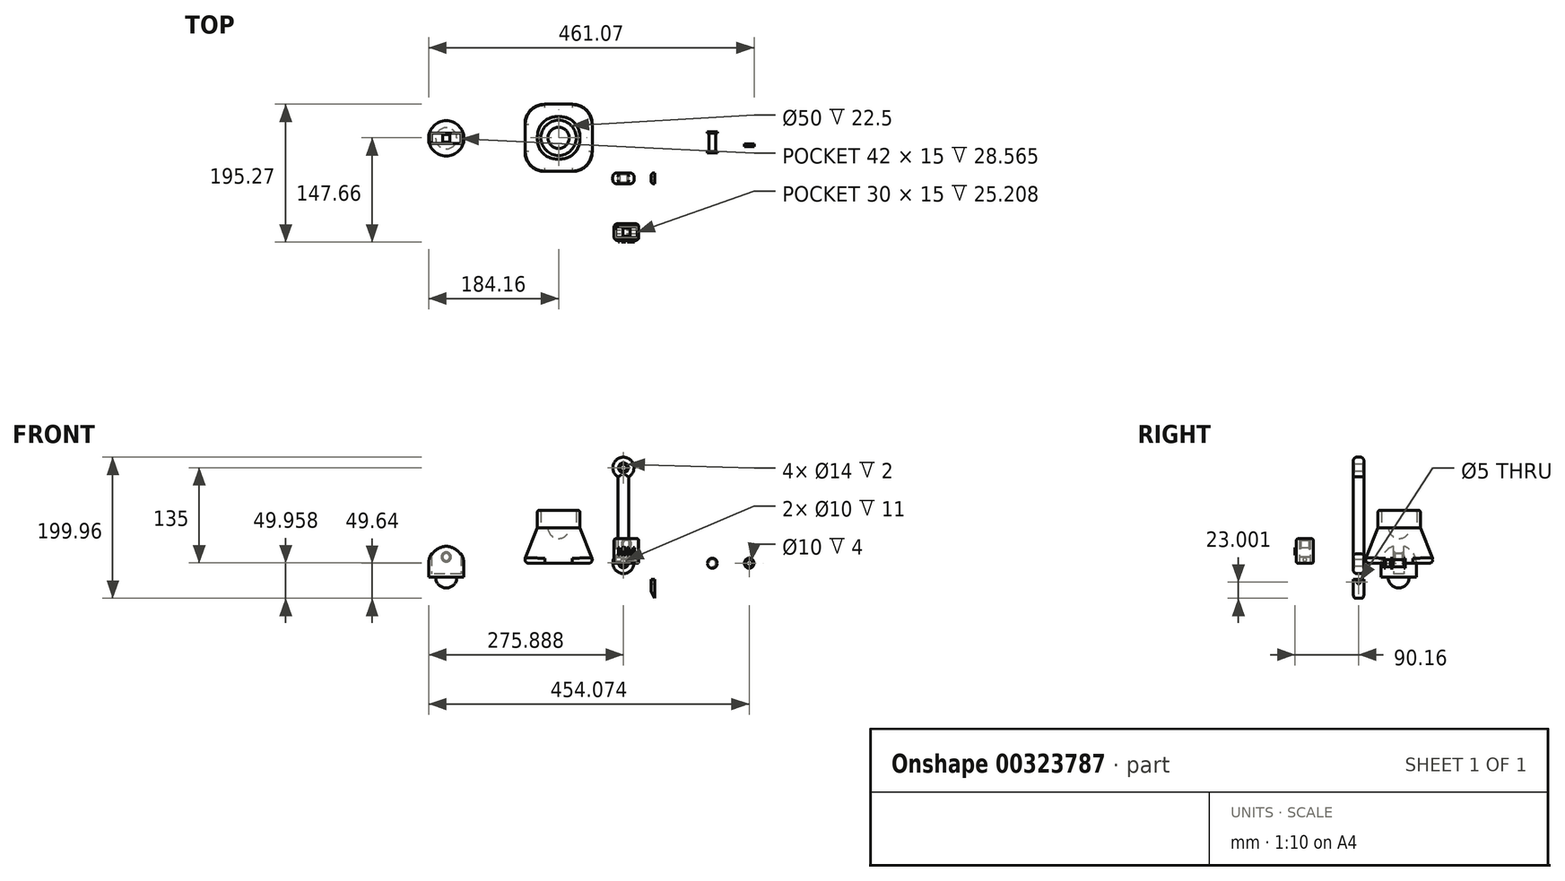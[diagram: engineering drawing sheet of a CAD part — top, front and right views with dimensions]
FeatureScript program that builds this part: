
annotation { "Feature Type Name" : "Feature", "Feature Type Description" : "" }
export const myFeature = defineFeature(function(context is Context, id is Id, definition is map)
    precondition{}
    {
        {
            var Q0;
            Q0=qCreatedBy(makeId("Top.planeOp"),FACE);
            var sketch = newSketch(context, id + "F0", { "sketchPlane" : qUnion([Q0])});
            skLineSegment(sketch, "E0.bottom", {"start": v(0, 0) * mm, "end": v(100, 0) * mm});
            skLineSegment(sketch, "E0.top", {"start": v(0, 100) * mm, "end": v(100, 100) * mm});
            skLineSegment(sketch, "E0.left", {"start": v(0, 0) * mm, "end": v(0, 100) * mm});
            skLineSegment(sketch, "E0.right", {"start": v(100, 0) * mm, "end": v(100, 100) * mm});
            skSolve(sketch);
        }
        {
            var Q0;
            Q0=makeQuery(id+"F0.imprint","IMPRINT",FACE,{"disambiguationData":[TD([[makeQuery(id+"F0.imprint","IMPRINT",EDGE,{"derivedFrom":sQuery(id+"F0.wireOp",EDGE,"E0.bottom")}),1.0]])]});
            cPlane(context, id + "F1", {"entities" : qUnion([Q0]), "cplaneType" : CPlaneType.OFFSET, "offset" : 50 * mm, "width" : 150 * mm, "height" : 150 * mm});
        }
        {
            var Q0;
            Q0=qCreatedBy(id+"F1.planeOp",FACE);
            var sketch = newSketch(context, id + "F2", { "sketchPlane" : qUnion([Q0])});
            skLineSegment(sketch, "E1.bottom", {"start": v(20, 80) * mm, "end": v(80, 80) * mm});
            skLineSegment(sketch, "E1.top", {"start": v(20, 20) * mm, "end": v(80, 20) * mm});
            skLineSegment(sketch, "E1.left", {"start": v(20, 80) * mm, "end": v(20, 20) * mm});
            skLineSegment(sketch, "E1.right", {"start": v(80, 80) * mm, "end": v(80, 20) * mm});
            skSolve(sketch);
        }
        {
            var Q0;
            Q0=makeQuery(id+"F0.imprint","IMPRINT",FACE,{"disambiguationData":[TD([[makeQuery(id+"F0.imprint","IMPRINT",EDGE,{"derivedFrom":sQuery(id+"F0.wireOp",EDGE,"E0.bottom")}),1.0]])]});
            var Q1;
            Q1=makeQuery(id+"F2.imprint","IMPRINT",FACE,{"disambiguationData":[TD([[makeQuery(id+"F2.imprint","IMPRINT",EDGE,{"derivedFrom":sQuery(id+"F2.wireOp",EDGE,"E1.bottom")}),-1.0]])]});
            loft(context, id + "F3", {"sheetProfilesArray" : [{ "sheetProfileEntities" : qUnion([Q0]) }, { "sheetProfileEntities" : qUnion([Q1]) }]});
        }
        {
            var Q0;
            Q0=makeQuery(id+"F3.opLoft","CAP_FACE",FACE,{"disambiguationData":[OSD([makeQuery(id+"F2.imprint","IMPRINT",FACE,{"disambiguationData":[TD([[makeQuery(id+"F2.imprint","IMPRINT",EDGE,{"derivedFrom":sQuery(id+"F2.wireOp",EDGE,"E1.bottom")}),-1.0]])]})])],"isStart":true});
            var sketch = newSketch(context, id + "F4", { "sketchPlane" : qUnion([Q0])});
            skLineSegment(sketch, "E2", {"start": v(50, 65) * mm, "end": v(50, 35) * mm});
            skArc(sketch, "E3", {"start": v(50, 35) * mm, "mid": v(65, 50) * mm, "end": v(50, 65) * mm});
            skPoint(sketch, "E4.orphan", {"position": v(50, 80) * mm});
            skPoint(sketch, "E5.orphan", {"position": v(50, 20) * mm});
            skSolve(sketch);
        }
        {
            var Q0;
            Q0=makeQuery(id+"F4.imprint","IMPRINT",FACE,{"disambiguationData":[TD([[makeQuery(id+"F4.imprint","IMPRINT",EDGE,{"derivedFrom":sQuery(id+"F4.wireOp",EDGE,"E2")}),1.0]])]});
            var Q1;
            Q1=sQuery(id+"F4.wireOp",EDGE,"E2");
            revolve(context, id + "F5", {"operationType" : NewBodyOperationType.REMOVE, "entities" : qUnion([Q0]), "axis" : qUnion([Q1]), "revolveType" : RevolveType.FULL, "oppositeDirection" : true});
        }
        {
            var Q0;
            Q0=makeQuery(id+"F3.opLoft","CAP_FACE",FACE,{"disambiguationData":[OSD([makeQuery(id+"F0.imprint","IMPRINT",FACE,{"disambiguationData":[TD([[makeQuery(id+"F0.imprint","IMPRINT",EDGE,{"derivedFrom":sQuery(id+"F0.wireOp",EDGE,"E0.bottom")}),1.0]])]})])],"isStart":true});
            fillet(context, id + "F6", {"entities" : qUnion([Q0]), "radius" : 5 * mm, "tangentPropagation" : true, "allowEdgeOverflow" : false});
        }
        {
            var Q0;
            Q0=makeQuery(id+"F3.opLoft","SWEPT_EDGE",EDGE,{"disambiguationData":[OSD([sQuery(id+"F0.wireOp",EDGE,"E0.bottom"),sQuery(id+"F0.wireOp",EDGE,"E0.right"),sQuery(id+"F2.wireOp",EDGE,"E1.top"),sQuery(id+"F2.wireOp",EDGE,"E1.right")])]});
            var Q1;
            Q1=makeQuery(id+"F3.opLoft","SWEPT_EDGE",EDGE,{"disambiguationData":[OSD([sQuery(id+"F0.wireOp",EDGE,"E0.top"),sQuery(id+"F0.wireOp",EDGE,"E0.right"),sQuery(id+"F2.wireOp",EDGE,"E1.bottom"),sQuery(id+"F2.wireOp",EDGE,"E1.right")])]});
            var Q2;
            Q2=makeQuery(id+"F3.opLoft","SWEPT_EDGE",EDGE,{"disambiguationData":[OSD([sQuery(id+"F0.wireOp",EDGE,"E0.top"),sQuery(id+"F0.wireOp",EDGE,"E0.left"),sQuery(id+"F2.wireOp",EDGE,"E1.bottom"),sQuery(id+"F2.wireOp",EDGE,"E1.left")])]});
            var Q3;
            Q3=makeQuery(id+"F3.opLoft","SWEPT_EDGE",EDGE,{"disambiguationData":[OSD([sQuery(id+"F0.wireOp",EDGE,"E0.bottom"),sQuery(id+"F0.wireOp",EDGE,"E0.left"),sQuery(id+"F2.wireOp",EDGE,"E1.top"),sQuery(id+"F2.wireOp",EDGE,"E1.left")])]});
            fillet(context, id + "F7", {"entities" : qUnion([Q0, Q1, Q2, Q3]), "radius" : 30 * mm, "tangentPropagation" : true, "allowEdgeOverflow" : false});
        }
        {
            var Q0;
            Q0=qCreatedBy(makeId("Top.planeOp"),FACE);
            var sketch = newSketch(context, id + "F8", { "sketchPlane" : qUnion([Q0])});
            skArc(sketch, "E6", {"start": v(184.89, 22.61) * mm, "mid": v(199.89, 37.61) * mm, "end": v(184.89, 52.61) * mm});
            skLineSegment(sketch, "E7", {"start": v(184.89, 22.61) * mm, "end": v(184.89, 52.61) * mm});
            skSolve(sketch);
        }
        {
            var Q0;
            Q0=qCreatedBy(makeId("Top.planeOp"),FACE);
            cPlane(context, id + "F9", {"entities" : qUnion([Q0]), "cplaneType" : CPlaneType.OFFSET, "offset" : 10 * mm, "width" : 150 * mm, "height" : 150 * mm});
        }
        {
            var Q0;
            Q0=qCreatedBy(id+"F9.planeOp",FACE);
            var sketch = newSketch(context, id + "F10", { "sketchPlane" : qUnion([Q0])});
            skLineSegment(sketch, "E8.bottom", {"start": v(177.39, 45.11) * mm, "end": v(192.39, 45.11) * mm});
            skLineSegment(sketch, "E8.top", {"start": v(177.39, 30.11) * mm, "end": v(192.39, 30.11) * mm});
            skLineSegment(sketch, "E8.left", {"start": v(177.39, 45.11) * mm, "end": v(177.39, 30.11) * mm});
            skLineSegment(sketch, "E8.right", {"start": v(192.39, 45.11) * mm, "end": v(192.39, 30.11) * mm});
            skSolve(sketch);
        }
        {
            var Q0;
            Q0=makeQuery(id+"F8.imprint","IMPRINT",FACE,{"disambiguationData":[TD([[makeQuery(id+"F8.imprint","IMPRINT",EDGE,{"derivedFrom":sQuery(id+"F8.wireOp",EDGE,"E6")}),1.0]])]});
            var Q1;
            Q1=sQuery(id+"F8.wireOp",EDGE,"E7");
            revolve(context, id + "F11", {"entities" : qUnion([Q0]), "axis" : qUnion([Q1]), "revolveType" : RevolveType.FULL});
        }
        {
            var Q0;
            Q0=qSketchRegion(id+"F10",true);
            extrude(context, id + "F12", {"entities" : qUnion([Q0]), "operationType" : NewBodyOperationType.ADD, "depth" : 120 * mm});
        }
        {
            var Q0;
            Q0=makeQuery(id+"F12.boolean.opBoolean","INTERSECT",EDGE,{"derivedFrom":[makeQuery(id+"F11.opRevolve","SWEPT_FACE",FACE,{"disambiguationData":[OSD([sQuery(id+"F8.wireOp",EDGE,"E6")])]}),makeQuery(id+"F12.opExtrude","SWEPT_FACE",FACE,{"disambiguationData":[OSD([sQuery(id+"F10.wireOp",EDGE,"E8.right")])]})]});
            var Q1;
            Q1=makeQuery(id+"F12.boolean.opBoolean","INTERSECT",EDGE,{"derivedFrom":[makeQuery(id+"F11.opRevolve","SWEPT_FACE",FACE,{"disambiguationData":[OSD([sQuery(id+"F8.wireOp",EDGE,"E6")])]}),makeQuery(id+"F12.opExtrude","SWEPT_FACE",FACE,{"disambiguationData":[OSD([sQuery(id+"F10.wireOp",EDGE,"E8.top")])]})]});
            var Q2;
            Q2=makeQuery(id+"F12.boolean.opBoolean","INTERSECT",EDGE,{"derivedFrom":[makeQuery(id+"F11.opRevolve","SWEPT_FACE",FACE,{"disambiguationData":[OSD([sQuery(id+"F8.wireOp",EDGE,"E6")])]}),makeQuery(id+"F12.opExtrude","SWEPT_FACE",FACE,{"disambiguationData":[OSD([sQuery(id+"F10.wireOp",EDGE,"E8.bottom")])]})]});
            var Q3;
            Q3=makeQuery(id+"F12.boolean.opBoolean","INTERSECT",EDGE,{"derivedFrom":[makeQuery(id+"F11.opRevolve","SWEPT_FACE",FACE,{"disambiguationData":[OSD([sQuery(id+"F8.wireOp",EDGE,"E6")])]}),makeQuery(id+"F12.opExtrude","SWEPT_FACE",FACE,{"disambiguationData":[OSD([sQuery(id+"F10.wireOp",EDGE,"E8.left")])]})]});
            var Q4;
            Q4=makeQuery(id+"F12.opExtrude","SWEPT_EDGE",EDGE,{"disambiguationData":[OSD([sQuery(id+"F10.wireOp",EDGE,"E8.bottom"),sQuery(id+"F10.wireOp",EDGE,"E8.left")])]});
            var Q5;
            Q5=makeQuery(id+"F12.opExtrude","SWEPT_EDGE",EDGE,{"disambiguationData":[OSD([sQuery(id+"F10.wireOp",EDGE,"E8.bottom"),sQuery(id+"F10.wireOp",EDGE,"E8.right")])]});
            var Q6;
            Q6=makeQuery(id+"F12.opExtrude","SWEPT_EDGE",EDGE,{"disambiguationData":[OSD([sQuery(id+"F10.wireOp",EDGE,"E8.top"),sQuery(id+"F10.wireOp",EDGE,"E8.right")])]});
            var Q7;
            Q7=makeQuery(id+"F12.opExtrude","SWEPT_EDGE",EDGE,{"disambiguationData":[OSD([sQuery(id+"F10.wireOp",EDGE,"E8.top"),sQuery(id+"F10.wireOp",EDGE,"E8.left")])]});
            fillet(context, id + "F13", {"entities" : qUnion([Q0, Q1, Q2, Q3, Q4, Q5, Q6, Q7]), "radius" : 5 * mm, "tangentPropagation" : true, "allowEdgeOverflow" : false});
        }
        {
            var Q0;
            Q0=makeQuery(id+"F12.opExtrude","CAP_EDGE",EDGE,{"disambiguationData":[OSD([sQuery(id+"F10.wireOp",EDGE,"E8.right")])],"isStart":false});
            cPoint(context, id + "F14", {"entities" : qUnion([Q0]), "parameter" : 0.5});
        }
        {
            var Q0;
            Q0=makeQuery(id+"F12.opExtrude","CAP_EDGE",EDGE,{"disambiguationData":[OSD([sQuery(id+"F10.wireOp",EDGE,"E8.left")])],"isStart":false});
            cPoint(context, id + "F15", {"entities" : qUnion([Q0]), "parameter" : 0.5});
        }
        {
            var Q0;
            {var subQ0=makeQuery(id+"F12.opExtrude","SWEPT_FACE",FACE,{"disambiguationData":[OSD([sQuery(id+"F10.wireOp",EDGE,"E8.left")])]});Q0=makeQuery(id+"F13.opFillet","BLEND_EDGE",EDGE,{"blendedFrom":[makeQuery(id+"F12.boolean.opBoolean","INTERSECT",EDGE,{"derivedFrom":[makeQuery(id+"F11.opRevolve","SWEPT_FACE",FACE,{"disambiguationData":[OSD([sQuery(id+"F8.wireOp",EDGE,"E6")])]}),subQ0]}),subQ0],"blendedInto":[subQ0]});}
            cPoint(context, id + "F16", {"entities" : qUnion([Q0]), "parameter" : 0.5});
        }
        {
            var Q0;
            Q0=qCreatedBy(id+"F14",VERTEX);
            var Q1;
            Q1=qCreatedBy(id+"F15",VERTEX);
            var Q2;
            Q2=qCreatedBy(id+"F16",VERTEX);
            cPlane(context, id + "F17", {"entities" : qUnion([Q0, Q1, Q2]), "cplaneType" : CPlaneType.THREE_POINT, "offset" : 25 * mm, "width" : 150 * mm, "height" : 150 * mm});
        }
        {
            var Q0;
            Q0=qCreatedBy(id+"F17.planeOp",FACE);
            var sketch = newSketch(context, id + "F18", { "sketchPlane" : qUnion([Q0])});
            skCircle(sketch, "E9", {"center": v(-184.89, 137.5) * mm, "radius": 15 * mm});
            skSolve(sketch);
        }
        {
            var Q0;
            Q0=makeQuery(id+"F18.imprint","IMPRINT",FACE,{"disambiguationData":[TD([[makeQuery(id+"F18.imprint","IMPRINT",EDGE,{"derivedFrom":sQuery(id+"F18.wireOp",EDGE,"E9")}),1.0]])]});
            extrude(context, id + "F19", {"entities" : qUnion([Q0]), "operationType" : NewBodyOperationType.ADD, "depth" : 15 * mm, "symmetric" : true});
        }
        {
            var Q0;
            Q0=makeQuery(id+"F19.opExtrude","CAP_EDGE",EDGE,{"disambiguationData":[OSD([sQuery(id+"F18.wireOp",EDGE,"E9")])],"isStart":true});
            var Q1;
            Q1=makeQuery(id+"F19.opExtrude","CAP_EDGE",EDGE,{"disambiguationData":[OSD([sQuery(id+"F18.wireOp",EDGE,"E9")])],"isStart":false});
            fillet(context, id + "F20", {"entities" : qUnion([Q0, Q1]), "radius" : 5 * mm, "tangentPropagation" : true, "allowEdgeOverflow" : false});
        }
        {
            var Q0;
            Q0=makeQuery(id+"F19.boolean.opBoolean","MERGE",FACE,{"derivedFrom":[makeQuery(id+"F12.opExtrude","SWEPT_FACE",FACE,{"disambiguationData":[OSD([sQuery(id+"F10.wireOp",EDGE,"E8.top")])]}),makeQuery(id+"F19.opExtrude","CAP_FACE",FACE,{"disambiguationData":[OSD([sQuery(id+"F18.wireOp",EDGE,"E9")])],"isStart":true})]});
            var sketch = newSketch(context, id + "F21", { "sketchPlane" : qUnion([Q0])});
            skCircle(sketch, "E10", {"center": v(184.89, 137.5) * mm, "radius": 5 * mm});
            skCircle(sketch, "E11", {"center": v(184.89, 137.5) * mm, "radius": 7 * mm});
            skSolve(sketch);
        }
        {
            var Q0;
            Q0=sQuery(id+"F21.wireOp",VERTEX,"E10.center");
            var Q1;
            Q1=makeQuery(id+"F11.opRevolve","SWEPT_BODY",BODY,{"disambiguationData":[OSD([sQuery(id+"F8.wireOp",EDGE,"E6"),sQuery(id+"F8.wireOp",EDGE,"E7")])]});
            hole(context, id + "F22", {"style" : HoleStyle.SIMPLE, "endStyle" : HoleEndStyle.THROUGH, "holeDiameter" : 10 * mm, "tappedDepth" : 12 * mm, "tapClearance" : 3, "locations" : qUnion([Q0]), "scope" : qUnion([Q1])});
        }
        {
            var Q0;
            Q0=makeQuery(id+"F19.boolean.opBoolean","MERGE",FACE,{"derivedFrom":[makeQuery(id+"F12.opExtrude","SWEPT_FACE",FACE,{"disambiguationData":[OSD([sQuery(id+"F10.wireOp",EDGE,"E8.bottom")])]}),makeQuery(id+"F19.opExtrude","CAP_FACE",FACE,{"disambiguationData":[OSD([sQuery(id+"F18.wireOp",EDGE,"E9")])],"isStart":false})]});
            var sketch = newSketch(context, id + "F23", { "sketchPlane" : qUnion([Q0])});
            skCircle(sketch, "E12", {"center": v(-184.89, 137.5) * mm, "radius": 7 * mm});
            skSolve(sketch);
        }
        {
            var Q0;
            Q0=qSketchRegion(id+"F21",true);
            var Q1;
            Q1=qSketchRegion(id+"F23",true);
            extrude(context, id + "F24", {"entities" : qUnion([Q0, Q1]), "operationType" : NewBodyOperationType.REMOVE, "oppositeDirection" : true, "depth" : 2 * mm, "hasSecondDirection" : true, "secondDirectionOppositeDirection" : false, "secondDirectionDepth" : 2 * mm});
        }
        {
            var Q0;
            Q0=qCreatedBy(makeId("Top.planeOp"),FACE);
            var sketch = newSketch(context, id + "F25", { "sketchPlane" : qUnion([Q0])});
            skLineSegment(sketch, "E13.bottom", {"start": v(267.71, 58.7) * mm, "end": v(272.71, 58.7) * mm});
            skLineSegment(sketch, "E13.top", {"start": v(267.71, 28.7) * mm, "end": v(272.71, 28.7) * mm});
            skLineSegment(sketch, "E13.left", {"start": v(267.71, 58.7) * mm, "end": v(267.71, 28.7) * mm});
            skLineSegment(sketch, "E13.right", {"start": v(272.71, 56.7) * mm, "end": v(272.71, 30.7) * mm});
            skLineSegment(sketch, "E14.bottom", {"start": v(272.71, 58.7) * mm, "end": v(274.71, 58.7) * mm});
            skLineSegment(sketch, "E14.top", {"start": v(272.71, 56.7) * mm, "end": v(274.71, 56.7) * mm});
            skLineSegment(sketch, "E14.right", {"start": v(274.71, 58.7) * mm, "end": v(274.71, 56.7) * mm});
            skLineSegment(sketch, "E15.bottom", {"start": v(272.71, 28.7) * mm, "end": v(274.71, 28.7) * mm});
            skLineSegment(sketch, "E15.top", {"start": v(272.71, 30.7) * mm, "end": v(274.71, 30.7) * mm});
            skLineSegment(sketch, "E15.right", {"start": v(274.71, 28.7) * mm, "end": v(274.71, 30.7) * mm});
            skSolve(sketch);
        }
        {
            var Q0;
            Q0=makeQuery(id+"F25.imprint","IMPRINT",FACE,{"disambiguationData":[TD([[makeQuery(id+"F25.imprint","IMPRINT",EDGE,{"derivedFrom":sQuery(id+"F25.wireOp",EDGE,"E13.bottom")}),-1.0]])]});
            var Q1;
            Q1=sQuery(id+"F25.wireOp",EDGE,"E13.left");
            revolve(context, id + "F26", {"entities" : qUnion([Q0]), "axis" : qUnion([Q1]), "revolveType" : RevolveType.FULL});
        }
        {
            var Q0;
            Q0=qCreatedBy(id+"F17.planeOp",FACE);
            var sketch = newSketch(context, id + "F27", { "sketchPlane" : qUnion([Q0])});
            skCircle(sketch, "E16", {"center": v(-319.91, 0) * mm, "radius": 7 * mm});
            skCircle(sketch, "E17", {"center": v(-319.91, 0) * mm, "radius": 5 * mm});
            skSolve(sketch);
        }
        {
            var Q0;
            Q0=qSketchRegion(id+"F27",true);
            extrude(context, id + "F28", {"entities" : qUnion([Q0]), "depth" : 4 * mm});
        }
        {
            var Q0;
            Q0=qCreatedBy(makeId("Top.planeOp"),FACE);
            var sketch = newSketch(context, id + "F29", { "sketchPlane" : qUnion([Q0])});
            skArc(sketch, "E18", {"start": v(-109.16, 24.23) * mm, "mid": v(-84.16, 49.23) * mm, "end": v(-109.16, 74.23) * mm});
            skLineSegment(sketch, "E19", {"start": v(-109.16, 74.23) * mm, "end": v(-109.16, 24.23) * mm});
            skSolve(sketch);
        }
        {
            var Q0;
            Q0=makeQuery(id+"F29.imprint","IMPRINT",FACE,{"disambiguationData":[TD([[makeQuery(id+"F29.imprint","IMPRINT",EDGE,{"derivedFrom":sQuery(id+"F29.wireOp",EDGE,"E18")}),1.0]])]});
            var Q1;
            Q1=sQuery(id+"F29.wireOp",EDGE,"E19");
            revolve(context, id + "F30", {"entities" : qUnion([Q0]), "axis" : qUnion([Q1]), "revolveType" : RevolveType.ONE_DIRECTION, "angle" : 180 * degree});
        }
        {
            var Q0;
            Q0=qCreatedBy(makeId("Front.planeOp"),FACE);
            var sketch = newSketch(context, id + "F31", { "sketchPlane" : qUnion([Q0])});
            skLineSegment(sketch, "E20.left", {"start": v(134.23, 122.33) * mm, "end": v(134.23, 13.3) * mm});
            skLineSegment(sketch, "E20.right", {"start": v(149.23, 122.33) * mm, "end": v(149.23, 13.3) * mm});
            skArc(sketch, "E21", {"start": v(149.23, 122.33) * mm, "mid": v(141.73, 150.32) * mm, "end": v(134.23, 122.33) * mm});
            skArc(sketch, "E22", {"start": v(134.23, 13.3) * mm, "mid": v(141.73, -14.68) * mm, "end": v(149.23, 13.3) * mm});
            skSolve(sketch);
        }
        {
            var Q0;
            Q0=makeQuery(id+"F31.imprint","IMPRINT",FACE,{"disambiguationData":[TD([[makeQuery(id+"F31.imprint","IMPRINT",EDGE,{"derivedFrom":sQuery(id+"F31.wireOp",EDGE,"E20.left")}),1.0]])]});
            extrude(context, id + "F32", {"entities" : qUnion([Q0]), "depth" : 15 * mm});
        }
        {
            var Q0;
            Q0=makeQuery(id+"F32.opExtrude","CAP_FACE",FACE,{"disambiguationData":[OSD([sQuery(id+"F31.wireOp",EDGE,"E20.left"),sQuery(id+"F31.wireOp",EDGE,"E20.right"),sQuery(id+"F31.wireOp",EDGE,"E21"),sQuery(id+"F31.wireOp",EDGE,"E22")])],"isStart":false});
            var Q1;
            Q1=makeQuery(id+"F32.opExtrude","CAP_FACE",FACE,{"disambiguationData":[OSD([sQuery(id+"F31.wireOp",EDGE,"E20.left"),sQuery(id+"F31.wireOp",EDGE,"E20.right"),sQuery(id+"F31.wireOp",EDGE,"E21"),sQuery(id+"F31.wireOp",EDGE,"E22")])],"isStart":true});
            fillet(context, id + "F33", {"entities" : qUnion([Q0, Q1]), "radius" : 5 * mm, "tangentPropagation" : true, "allowEdgeOverflow" : false});
        }
        {
            var Q0;
            Q0=makeQuery(id+"F32.opExtrude","CAP_FACE",FACE,{"disambiguationData":[OSD([sQuery(id+"F31.wireOp",EDGE,"E20.left"),sQuery(id+"F31.wireOp",EDGE,"E20.right"),sQuery(id+"F31.wireOp",EDGE,"E21"),sQuery(id+"F31.wireOp",EDGE,"E22")])],"isStart":false});
            var sketch = newSketch(context, id + "F34", { "sketchPlane" : qUnion([Q0])});
            skCircle(sketch, "E23", {"center": v(141.73, 135.32) * mm, "radius": 5 * mm});
            skCircle(sketch, "E24", {"center": v(141.73, 0.32) * mm, "radius": 5 * mm});
            skCircle(sketch, "E25", {"center": v(141.73, 135.32) * mm, "radius": 7 * mm});
            skCircle(sketch, "E26", {"center": v(141.73, 0.32) * mm, "radius": 7 * mm});
            skSolve(sketch);
        }
        {
            var Q0;
            Q0=makeQuery(id+"F34.imprint","IMPRINT",FACE,{"disambiguationData":[TD([[makeQuery(id+"F34.imprint","IMPRINT",EDGE,{"derivedFrom":sQuery(id+"F34.wireOp",EDGE,"E23")}),1.0]])]});
            var Q1;
            Q1=makeQuery(id+"F34.imprint","IMPRINT",FACE,{"disambiguationData":[TD([[makeQuery(id+"F34.imprint","IMPRINT",EDGE,{"derivedFrom":sQuery(id+"F34.wireOp",EDGE,"E24")}),1.0]])]});
            extrude(context, id + "F35", {"entities" : qUnion([Q0, Q1]), "operationType" : NewBodyOperationType.REMOVE, "endBound" : BoundingType.THROUGH_ALL, "oppositeDirection" : true, "depth" : 25 * mm});
        }
        {
            var Q0;
            Q0=qSketchRegion(id+"F34",true);
            extrude(context, id + "F36", {"entities" : qUnion([Q0]), "operationType" : NewBodyOperationType.REMOVE, "oppositeDirection" : true, "depth" : 2 * mm});
        }
        {
            var Q0;
            Q0=makeQuery(id+"F32.opExtrude","CAP_FACE",FACE,{"disambiguationData":[OSD([sQuery(id+"F31.wireOp",EDGE,"E20.left"),sQuery(id+"F31.wireOp",EDGE,"E20.right"),sQuery(id+"F31.wireOp",EDGE,"E21"),sQuery(id+"F31.wireOp",EDGE,"E22")])],"isStart":true});
            var sketch = newSketch(context, id + "F37", { "sketchPlane" : qUnion([Q0])});
            skCircle(sketch, "E27", {"center": v(-141.73, 135.32) * mm, "radius": 7 * mm});
            skCircle(sketch, "E28", {"center": v(-141.73, 0.32) * mm, "radius": 7 * mm});
            skSolve(sketch);
        }
        {
            var Q0;
            Q0=qSketchRegion(id+"F37",true);
            extrude(context, id + "F38", {"entities" : qUnion([Q0]), "operationType" : NewBodyOperationType.REMOVE, "oppositeDirection" : true, "depth" : 2 * mm});
        }
        {
            var Q0;
            Q0=makeQuery(id+"F30.opRevolve","CAP_FACE",FACE,{"disambiguationData":[OSD([sQuery(id+"F29.wireOp",EDGE,"E18"),sQuery(id+"F29.wireOp",EDGE,"E19")])],"isStart":true});
            var sketch = newSketch(context, id + "F39", { "sketchPlane" : qUnion([Q0])});
            skLineSegment(sketch, "E29.bottom", {"start": v(-88.16, -56.73) * mm, "end": v(-130.16, -56.73) * mm});
            skLineSegment(sketch, "E29.top", {"start": v(-88.16, -41.73) * mm, "end": v(-130.16, -41.73) * mm});
            skLineSegment(sketch, "E29.left", {"start": v(-88.16, -56.73) * mm, "end": v(-88.16, -41.73) * mm});
            skLineSegment(sketch, "E29.right", {"start": v(-130.16, -56.73) * mm, "end": v(-130.16, -41.73) * mm});
            skSolve(sketch);
        }
        {
            var Q0;
            Q0=makeQuery(id+"F39.imprint","IMPRINT",FACE,{"disambiguationData":[TD([[makeQuery(id+"F39.imprint","IMPRINT",EDGE,{"derivedFrom":sQuery(id+"F39.wireOp",EDGE,"E29.bottom")}),1.0]])]});
            var Q1;
            Q1=makeQuery(id+"F39.imprint","IMPRINT",FACE,{"disambiguationData":[TD([[makeQuery(id+"F39.imprint","IMPRINT",EDGE,{"derivedFrom":sQuery(id+"F39.wireOp",EDGE,"E29.bottom")}),-1.0]])]});
            extrude(context, id + "F40", {"entities" : qUnion([Q0, Q1]), "operationType" : NewBodyOperationType.ADD, "depth" : 20 * mm});
        }
        {
            var Q0;
            Q0=makeQuery(id+"F40.opExtrude","CAP_FACE",FACE,{"disambiguationData":[OSD([sQuery(id+"F29.wireOp",EDGE,"E18")])],"isStart":false});
            var sketch = newSketch(context, id + "F41", { "sketchPlane" : qUnion([Q0])});
            skArc(sketch, "E30", {"start": v(-109.16, -34.23) * mm, "mid": v(-124.16, -49.23) * mm, "end": v(-109.16, -64.23) * mm});
            skLineSegment(sketch, "E31", {"start": v(-109.16, -64.23) * mm, "end": v(-109.16, -34.23) * mm});
            skSolve(sketch);
        }
        {
            var Q0;
            Q0=makeQuery(id+"F41.imprint","IMPRINT",FACE,{"disambiguationData":[TD([[makeQuery(id+"F41.imprint","IMPRINT",EDGE,{"derivedFrom":sQuery(id+"F41.wireOp",EDGE,"E30")}),1.0]])]});
            var Q1;
            Q1=sQuery(id+"F41.wireOp",EDGE,"E31");
            revolve(context, id + "F42", {"operationType" : NewBodyOperationType.ADD, "entities" : qUnion([Q0]), "axis" : qUnion([Q1]), "revolveType" : RevolveType.FULL});
        }
        {
            var Q0;
            Q0=qSketchRegion(id+"F39",true);
            extrude(context, id + "F43", {"entities" : qUnion([Q0]), "operationType" : NewBodyOperationType.REMOVE, "endBound" : BoundingType.THROUGH_ALL, "oppositeDirection" : true, "depth" : 25 * mm, "hasSecondDirection" : true, "secondDirectionOppositeDirection" : false, "secondDirectionDepth" : 15 * mm});
        }
        {
            var Q0;
            Q0=makeQuery(id+"F43.boolean.opBoolean","COPY",FACE,{"derivedFrom":makeQuery(id+"F43.opExtrude","SWEPT_FACE",FACE,{"disambiguationData":[OSD([sQuery(id+"F39.wireOp",EDGE,"E29.top")])]})});
            var sketch = newSketch(context, id + "F44", { "sketchPlane" : qUnion([Q0])});
            skCircle(sketch, "E32", {"center": v(109.16, 8.85) * mm, "radius": 7 * mm});
            skPoint(sketch, "E32.centerSnap0", {"position": v(109.16, 23.85) * mm});
            skPoint(sketch, "E32.centerSnap1", {"position": v(130.16, -1.85) * mm});
            skSolve(sketch);
        }
        {
            var Q0;
            Q0=makeQuery(id+"F44.imprint","IMPRINT",FACE,{"disambiguationData":[TD([[makeQuery(id+"F44.imprint","IMPRINT",EDGE,{"derivedFrom":sQuery(id+"F44.wireOp",EDGE,"E32")}),1.0]])]});
            extrude(context, id + "F45", {"entities" : qUnion([Q0]), "operationType" : NewBodyOperationType.ADD, "depth" : 2 * mm});
        }
        {
            var Q0;
            Q0=makeQuery(id+"F45.opExtrude","CAP_FACE",FACE,{"disambiguationData":[OSD([sQuery(id+"F44.wireOp",EDGE,"E32")])],"isStart":false});
            var sketch = newSketch(context, id + "F46", { "sketchPlane" : qUnion([Q0])});
            skCircle(sketch, "E33", {"center": v(109.16, 8.85) * mm, "radius": 5 * mm});
            skSolve(sketch);
        }
        {
            var Q0;
            Q0=makeQuery(id+"F46.imprint","IMPRINT",FACE,{"disambiguationData":[TD([[makeQuery(id+"F46.imprint","IMPRINT",EDGE,{"derivedFrom":sQuery(id+"F46.wireOp",EDGE,"E33")}),1.0]])]});
            extrude(context, id + "F47", {"entities" : qUnion([Q0]), "operationType" : NewBodyOperationType.ADD, "endBound" : BoundingType.UP_TO_NEXT, "depth" : 25 * mm});
        }
        {
            var Q0;
            Q0=qCreatedBy(makeId("Top.planeOp"),FACE);
            var sketch = newSketch(context, id + "F48", { "sketchPlane" : qUnion([Q0])});
            skLineSegment(sketch, "E34.bottom", {"start": v(203.21, -84.7) * mm, "end": v(208.21, -84.7) * mm});
            skLineSegment(sketch, "E34.top", {"start": v(203.21, -99.7) * mm, "end": v(208.21, -99.7) * mm});
            skLineSegment(sketch, "E34.left", {"start": v(198.21, -89.7) * mm, "end": v(198.21, -94.7) * mm});
            skLineSegment(sketch, "E34.right", {"start": v(213.21, -89.7) * mm, "end": v(213.21, -94.7) * mm});
            skPoint(sketch, "E35.visualSharp", {"position": v(198.21, -84.7) * mm});
            skArc(sketch, "E35.filletArc", {"start": v(203.21, -84.7) * mm, "mid": v(199.68, -86.16) * mm, "end": v(198.21, -89.7) * mm});
            skPoint(sketch, "E36.visualSharp", {"position": v(213.21, -84.7) * mm});
            skArc(sketch, "E36.filletArc", {"start": v(213.21, -89.7) * mm, "mid": v(211.75, -86.16) * mm, "end": v(208.21, -84.7) * mm});
            skPoint(sketch, "E37.visualSharp", {"position": v(213.21, -99.7) * mm});
            skArc(sketch, "E37.filletArc", {"start": v(208.21, -99.7) * mm, "mid": v(211.75, -98.23) * mm, "end": v(213.21, -94.7) * mm});
            skPoint(sketch, "E38.visualSharp", {"position": v(198.21, -99.7) * mm});
            skArc(sketch, "E38.filletArc", {"start": v(198.21, -94.7) * mm, "mid": v(199.68, -98.23) * mm, "end": v(203.21, -99.7) * mm});
            skLineSegment(sketch, "E39.bottom", {"start": v(192.71, -74.2) * mm, "end": v(218.71, -74.2) * mm});
            skLineSegment(sketch, "E39.top", {"start": v(192.71, -110.2) * mm, "end": v(218.71, -110.2) * mm});
            skLineSegment(sketch, "E39.left", {"start": v(187.71, -79.2) * mm, "end": v(187.71, -105.2) * mm});
            skLineSegment(sketch, "E39.right", {"start": v(223.71, -79.2) * mm, "end": v(223.71, -105.2) * mm});
            skPoint(sketch, "E40.visualSharp", {"position": v(187.71, -74.2) * mm});
            skArc(sketch, "E40.filletArc", {"start": v(192.71, -74.2) * mm, "mid": v(189.18, -75.66) * mm, "end": v(187.71, -79.2) * mm});
            skPoint(sketch, "E41.visualSharp", {"position": v(223.71, -74.2) * mm});
            skArc(sketch, "E41.filletArc", {"start": v(223.71, -79.2) * mm, "mid": v(222.25, -75.66) * mm, "end": v(218.71, -74.2) * mm});
            skPoint(sketch, "E42.visualSharp", {"position": v(223.71, -110.2) * mm});
            skArc(sketch, "E42.filletArc", {"start": v(218.71, -110.2) * mm, "mid": v(222.25, -108.73) * mm, "end": v(223.71, -105.2) * mm});
            skPoint(sketch, "E43.visualSharp", {"position": v(187.71, -110.2) * mm});
            skArc(sketch, "E43.filletArc", {"start": v(187.71, -105.2) * mm, "mid": v(189.18, -108.73) * mm, "end": v(192.71, -110.2) * mm});
            skSolve(sketch);
        }
        {
            var Q0;
            Q0=makeQuery(id+"F48.imprint","IMPRINT",FACE,{"disambiguationData":[TD([[makeQuery(id+"F48.imprint","IMPRINT",EDGE,{"derivedFrom":sQuery(id+"F48.wireOp",EDGE,"E34.bottom")}),1.0]])]});
            extrude(context, id + "F49", {"entities" : qUnion([Q0]), "depth" : 20 * mm});
        }
        {
            var Q0;
            Q0=makeQuery(id+"F49.opExtrude","CAP_EDGE",EDGE,{"disambiguationData":[OSD([sQuery(id+"F48.wireOp",EDGE,"E39.left")])],"isStart":false});
            fillet(context, id + "F50", {"entities" : qUnion([Q0]), "radius" : 10 * mm, "tangentPropagation" : true, "allowEdgeOverflow" : false});
        }
        {
            var Q0;
            Q0=makeQuery(id+"F49.opExtrude","CAP_EDGE",EDGE,{"disambiguationData":[OSD([sQuery(id+"F48.wireOp",EDGE,"E34.top")])],"isStart":true});
            var Q1;
            Q1=makeQuery(id+"F49.opExtrude","CAP_EDGE",EDGE,{"disambiguationData":[OSD([sQuery(id+"F48.wireOp",EDGE,"E37.filletArc")])],"isStart":true});
            fillet(context, id + "F51", {"entities" : qUnion([Q0, Q1]), "radius" : 5 * mm, "tangentPropagation" : true, "allowEdgeOverflow" : false});
        }
        {
            var Q0;
            Q0=makeQuery(id+"F11.opRevolve","SWEPT_BODY",BODY,{"disambiguationData":[OSD([sQuery(id+"F8.wireOp",EDGE,"E6"),sQuery(id+"F8.wireOp",EDGE,"E7")])]});
            deleteBodies(context, id + "F52", {"entities" : qUnion([Q0])});
        }
        {
            var Q0;
            Q0=makeQuery(id+"F49.opExtrude","SWEPT_BODY",BODY,{"disambiguationData":[OSD([sQuery(id+"F48.wireOp",EDGE,"E34.bottom"),sQuery(id+"F48.wireOp",EDGE,"E34.top"),sQuery(id+"F48.wireOp",EDGE,"E34.left"),sQuery(id+"F48.wireOp",EDGE,"E34.right"),sQuery(id+"F48.wireOp",EDGE,"E35.filletArc"),sQuery(id+"F48.wireOp",EDGE,"E36.filletArc"),sQuery(id+"F48.wireOp",EDGE,"E37.filletArc"),sQuery(id+"F48.wireOp",EDGE,"E38.filletArc"),sQuery(id+"F48.wireOp",EDGE,"E39.bottom"),sQuery(id+"F48.wireOp",EDGE,"E39.top"),sQuery(id+"F48.wireOp",EDGE,"E39.left"),sQuery(id+"F48.wireOp",EDGE,"E39.right"),sQuery(id+"F48.wireOp",EDGE,"E40.filletArc"),sQuery(id+"F48.wireOp",EDGE,"E41.filletArc"),sQuery(id+"F48.wireOp",EDGE,"E42.filletArc"),sQuery(id+"F48.wireOp",EDGE,"E43.filletArc")])]});
            deleteBodies(context, id + "F53", {"entities" : qUnion([Q0])});
        }
        {
            var Q0;
            Q0=makeQuery(id+"F43.boolean.opBoolean","COPY",FACE,{"derivedFrom":makeQuery(id+"F43.opExtrude","SWEPT_FACE",FACE,{"disambiguationData":[OSD([sQuery(id+"F39.wireOp",EDGE,"E29.bottom")])]})});
            var sketch = newSketch(context, id + "F54", { "sketchPlane" : qUnion([Q0])});
            skCircle(sketch, "E44", {"center": v(-109.16, 8.85) * mm, "radius": 7 * mm});
            skSolve(sketch);
        }
        {
            var Q0;
            Q0=makeQuery(id+"F54.imprint","IMPRINT",FACE,{"disambiguationData":[TD([[makeQuery(id+"F54.imprint","IMPRINT",EDGE,{"derivedFrom":sQuery(id+"F54.wireOp",EDGE,"E44")}),1.0]])]});
            extrude(context, id + "F55", {"entities" : qUnion([Q0]), "operationType" : NewBodyOperationType.ADD, "depth" : 2 * mm});
        }
        {
            var Q0;
            Q0=qCreatedBy(makeId("Top.planeOp"),FACE);
            var sketch = newSketch(context, id + "F56", { "sketchPlane" : qUnion([Q0])});
            skLineSegment(sketch, "E45.bottom", {"start": v(133.56, -71.66) * mm, "end": v(158.56, -71.66) * mm});
            skLineSegment(sketch, "E45.top", {"start": v(133.56, -95.66) * mm, "end": v(158.56, -95.66) * mm});
            skLineSegment(sketch, "E45.left", {"start": v(128.56, -76.66) * mm, "end": v(128.56, -90.66) * mm});
            skLineSegment(sketch, "E45.right", {"start": v(163.56, -76.66) * mm, "end": v(163.56, -90.66) * mm});
            skPoint(sketch, "E46.visualSharp", {"position": v(163.56, -71.66) * mm});
            skArc(sketch, "E46.filletArc", {"start": v(163.56, -76.66) * mm, "mid": v(162.1, -73.13) * mm, "end": v(158.56, -71.66) * mm});
            skPoint(sketch, "E47.visualSharp", {"position": v(163.56, -95.66) * mm});
            skArc(sketch, "E47.filletArc", {"start": v(158.56, -95.66) * mm, "mid": v(162.1, -94.2) * mm, "end": v(163.56, -90.66) * mm});
            skPoint(sketch, "E48.visualSharp", {"position": v(128.56, -95.66) * mm});
            skArc(sketch, "E48.filletArc", {"start": v(128.56, -90.66) * mm, "mid": v(130.03, -94.2) * mm, "end": v(133.56, -95.66) * mm});
            skPoint(sketch, "E49.visualSharp", {"position": v(128.56, -71.66) * mm});
            skArc(sketch, "E49.filletArc", {"start": v(133.56, -71.66) * mm, "mid": v(130.03, -73.13) * mm, "end": v(128.56, -76.66) * mm});
            skPoint(sketch, "E50.firstSnap0", {"position": v(146.06, -71.66) * mm});
            skLineSegment(sketch, "E50.bottom", {"start": v(131.06, -76.16) * mm, "end": v(161.06, -76.16) * mm});
            skLineSegment(sketch, "E50.top", {"start": v(131.06, -91.16) * mm, "end": v(161.06, -91.16) * mm});
            skLineSegment(sketch, "E50.left", {"start": v(131.06, -76.16) * mm, "end": v(131.06, -91.16) * mm});
            skLineSegment(sketch, "E50.right", {"start": v(161.06, -76.16) * mm, "end": v(161.06, -91.16) * mm});
            skSolve(sketch);
        }
        {
            var Q0;
            Q0=makeQuery(id+"F56.imprint","IMPRINT",FACE,{"disambiguationData":[TD([[makeQuery(id+"F56.imprint","IMPRINT",EDGE,{"derivedFrom":sQuery(id+"F56.wireOp",EDGE,"E45.bottom")}),-1.0]])]});
            extrude(context, id + "F57", {"entities" : qUnion([Q0]), "depth" : 35 * mm});
        }
        {
            var Q0;
            Q0=makeQuery(id+"F57.opExtrude","SWEPT_FACE",FACE,{"disambiguationData":[OSD([sQuery(id+"F56.wireOp",EDGE,"E50.bottom")])]});
            var sketch = newSketch(context, id + "F58", { "sketchPlane" : qUnion([Q0])});
            skCircle(sketch, "E51", {"center": v(146.06, 27.5) * mm, "radius": 5 * mm});
            skCircle(sketch, "E52", {"center": v(146.06, 27.5) * mm, "radius": 7 * mm});
            skSolve(sketch);
        }
        {
            var Q0;
            Q0=makeQuery(id+"F58.imprint","IMPRINT",FACE,{"disambiguationData":[TD([[makeQuery(id+"F58.imprint","IMPRINT",EDGE,{"derivedFrom":sQuery(id+"F58.wireOp",EDGE,"E51")}),1.0]])]});
            extrude(context, id + "F59", {"entities" : qUnion([Q0]), "operationType" : NewBodyOperationType.ADD, "endBound" : BoundingType.UP_TO_NEXT, "depth" : 25 * mm});
        }
        {
            var Q0;
            Q0=makeQuery(id+"F58.imprint","IMPRINT",FACE,{"disambiguationData":[TD([[makeQuery(id+"F58.imprint","IMPRINT",EDGE,{"derivedFrom":sQuery(id+"F58.wireOp",EDGE,"E51")}),-1.0]])]});
            extrude(context, id + "F60", {"entities" : qUnion([Q0]), "operationType" : NewBodyOperationType.ADD, "depth" : 2 * mm});
        }
        {
            var Q0;
            Q0=makeQuery(id+"F57.opExtrude","SWEPT_FACE",FACE,{"disambiguationData":[OSD([sQuery(id+"F56.wireOp",EDGE,"E50.top")])]});
            var sketch = newSketch(context, id + "F61", { "sketchPlane" : qUnion([Q0])});
            skCircle(sketch, "E53", {"center": v(-146.06, 27.5) * mm, "radius": 7 * mm});
            skSolve(sketch);
        }
        {
            var Q0;
            Q0=makeQuery(id+"F61.imprint","IMPRINT",FACE,{"disambiguationData":[TD([[makeQuery(id+"F61.imprint","IMPRINT",EDGE,{"derivedFrom":sQuery(id+"F61.wireOp",EDGE,"E53")}),1.0]])]});
            extrude(context, id + "F62", {"entities" : qUnion([Q0]), "operationType" : NewBodyOperationType.ADD, "depth" : 2 * mm});
        }
        {
            var Q0;
            Q0=qCreatedBy(makeId("Front.planeOp"),FACE);
            var sketch = newSketch(context, id + "F63", { "sketchPlane" : qUnion([Q0])});
            skLineSegment(sketch, "E54", {"start": v(181.27, -22.64) * mm, "end": v(181.27, -40.64) * mm});
            skLineSegment(sketch, "E55", {"start": v(181.27, -40.64) * mm, "end": v(186.27, -49.64) * mm});
            skLineSegment(sketch, "E56", {"start": v(186.27, -49.64) * mm, "end": v(186.27, -22.64) * mm});
            skLineSegment(sketch, "E57", {"start": v(186.27, -22.64) * mm, "end": v(181.27, -22.64) * mm});
            skSolve(sketch);
        }
        {
            var Q0;
            Q0=makeQuery(id+"F63.imprint","IMPRINT",FACE,{"disambiguationData":[TD([[makeQuery(id+"F63.imprint","IMPRINT",EDGE,{"derivedFrom":sQuery(id+"F63.wireOp",EDGE,"E54")}),1.0]])]});
            extrude(context, id + "F64", {"entities" : qUnion([Q0]), "depth" : 15 * mm});
        }
        {
            var Q0;
            Q0=makeQuery(id+"F57.opExtrude","SWEPT_FACE",FACE,{"disambiguationData":[OSD([sQuery(id+"F56.wireOp",EDGE,"E50.left")])]});
            var sketch = newSketch(context, id + "F65", { "sketchPlane" : qUnion([Q0])});
            skCircle(sketch, "E58", {"center": v(-83.66, 5) * mm, "radius": 2.5 * mm});
            skPoint(sketch, "E58.centerSnap0", {"position": v(-83.66, 0) * mm});
            skLineSegment(sketch, "E59.bottom", {"start": v(-91.16, 9.75) * mm, "end": v(-76.16, 9.75) * mm});
            skLineSegment(sketch, "E59.top", {"start": v(-91.16, 9) * mm, "end": v(-76.16, 9) * mm});
            skLineSegment(sketch, "E59.left", {"start": v(-91.16, 9.75) * mm, "end": v(-91.16, 9) * mm});
            skLineSegment(sketch, "E59.right", {"start": v(-76.16, 9.75) * mm, "end": v(-76.16, 9) * mm});
            skSolve(sketch);
        }
        {
            var Q0;
            Q0=makeQuery(id+"F65.imprint","IMPRINT",FACE,{"disambiguationData":[TD([[makeQuery(id+"F65.imprint","IMPRINT",EDGE,{"derivedFrom":sQuery(id+"F65.wireOp",EDGE,"E58")}),1.0]])]});
            var Q1;
            Q1=makeQuery(id+"F65.imprint","IMPRINT",FACE,{"disambiguationData":[TD([[makeQuery(id+"F65.imprint","IMPRINT",EDGE,{"derivedFrom":sQuery(id+"F65.wireOp",EDGE,"E59.bottom")}),-1.0]])]});
            extrude(context, id + "F66", {"entities" : qUnion([Q0, Q1]), "operationType" : NewBodyOperationType.ADD, "endBound" : BoundingType.UP_TO_NEXT, "depth" : 25 * mm});
        }
        {
            var Q0;
            Q0=makeQuery(id+"F64.opExtrude","SWEPT_FACE",FACE,{"disambiguationData":[OSD([sQuery(id+"F63.wireOp",EDGE,"E56")])]});
            var sketch = newSketch(context, id + "F67", { "sketchPlane" : qUnion([Q0])});
            skCircle(sketch, "E60", {"center": v(-7.5, -26.64) * mm, "radius": 2.5 * mm});
            skPoint(sketch, "E60.centerSnap0", {"position": v(-7.5, -22.64) * mm});
            skSolve(sketch);
        }
        {
            var Q0;
            Q0=makeQuery(id+"F67.imprint","IMPRINT",FACE,{"disambiguationData":[TD([[makeQuery(id+"F67.imprint","IMPRINT",EDGE,{"derivedFrom":sQuery(id+"F67.wireOp",EDGE,"E60")}),1.0]])]});
            extrude(context, id + "F68", {"entities" : qUnion([Q0]), "operationType" : NewBodyOperationType.REMOVE, "endBound" : BoundingType.UP_TO_NEXT, "oppositeDirection" : true, "depth" : 25 * mm});
        }
        {
            var Q0;
            Q0=makeQuery(id+"F57.opExtrude","CAP_EDGE",EDGE,{"disambiguationData":[OSD([sQuery(id+"F56.wireOp",EDGE,"E45.top")])],"isStart":true});
            var Q1;
            Q1=makeQuery(id+"F57.opExtrude","CAP_EDGE",EDGE,{"disambiguationData":[OSD([sQuery(id+"F56.wireOp",EDGE,"E45.right")])],"isStart":true});
            var Q2;
            Q2=makeQuery(id+"F57.opExtrude","CAP_EDGE",EDGE,{"disambiguationData":[OSD([sQuery(id+"F56.wireOp",EDGE,"E47.filletArc")])],"isStart":true});
            var Q3;
            Q3=makeQuery(id+"F57.opExtrude","CAP_EDGE",EDGE,{"disambiguationData":[OSD([sQuery(id+"F56.wireOp",EDGE,"E45.bottom")])],"isStart":true});
            var Q4;
            Q4=makeQuery(id+"F57.opExtrude","CAP_EDGE",EDGE,{"disambiguationData":[OSD([sQuery(id+"F56.wireOp",EDGE,"E49.filletArc")])],"isStart":true});
            var Q5;
            Q5=makeQuery(id+"F57.opExtrude","CAP_EDGE",EDGE,{"disambiguationData":[OSD([sQuery(id+"F56.wireOp",EDGE,"E45.left")])],"isStart":true});
            var Q6;
            Q6=makeQuery(id+"F57.opExtrude","CAP_EDGE",EDGE,{"disambiguationData":[OSD([sQuery(id+"F56.wireOp",EDGE,"E48.filletArc")])],"isStart":true});
            var Q7;
            Q7=makeQuery(id+"F57.opExtrude","CAP_EDGE",EDGE,{"disambiguationData":[OSD([sQuery(id+"F56.wireOp",EDGE,"E46.filletArc")])],"isStart":true});
            fillet(context, id + "F69", {"entities" : qUnion([Q0, Q1, Q2, Q3, Q4, Q5, Q6, Q7]), "radius" : 2 * mm, "tangentPropagation" : true, "allowEdgeOverflow" : false});
        }
        {
            var Q0;
            Q0=makeQuery(id+"F57.opExtrude","CAP_EDGE",EDGE,{"disambiguationData":[OSD([sQuery(id+"F56.wireOp",EDGE,"E45.top")])],"isStart":false});
            var Q1;
            Q1=makeQuery(id+"F57.opExtrude","CAP_EDGE",EDGE,{"disambiguationData":[OSD([sQuery(id+"F56.wireOp",EDGE,"E46.filletArc")])],"isStart":false});
            var Q2;
            Q2=makeQuery(id+"F57.opExtrude","CAP_EDGE",EDGE,{"disambiguationData":[OSD([sQuery(id+"F56.wireOp",EDGE,"E47.filletArc")])],"isStart":false});
            var Q3;
            Q3=makeQuery(id+"F57.opExtrude","CAP_EDGE",EDGE,{"disambiguationData":[OSD([sQuery(id+"F56.wireOp",EDGE,"E48.filletArc")])],"isStart":false});
            var Q4;
            Q4=makeQuery(id+"F57.opExtrude","CAP_EDGE",EDGE,{"disambiguationData":[OSD([sQuery(id+"F56.wireOp",EDGE,"E45.left")])],"isStart":false});
            var Q5;
            Q5=makeQuery(id+"F57.opExtrude","CAP_EDGE",EDGE,{"disambiguationData":[OSD([sQuery(id+"F56.wireOp",EDGE,"E45.bottom")])],"isStart":false});
            var Q6;
            Q6=makeQuery(id+"F57.opExtrude","CAP_EDGE",EDGE,{"disambiguationData":[OSD([sQuery(id+"F56.wireOp",EDGE,"E49.filletArc")])],"isStart":false});
            fillet(context, id + "F70", {"entities" : qUnion([Q0, Q1, Q2, Q3, Q4, Q5, Q6]), "radius" : 3 * mm, "tangentPropagation" : true, "allowEdgeOverflow" : false});
        }
        {
            var Q0;
            Q0=makeQuery(id+"F64.opExtrude","CAP_EDGE",EDGE,{"disambiguationData":[OSD([sQuery(id+"F63.wireOp",EDGE,"E55")])],"isStart":false});
            var Q1;
            Q1=makeQuery(id+"F64.opExtrude","CAP_EDGE",EDGE,{"disambiguationData":[OSD([sQuery(id+"F63.wireOp",EDGE,"E55")])],"isStart":true});
            var Q2;
            Q2=makeQuery(id+"F64.opExtrude","SWEPT_EDGE",EDGE,{"disambiguationData":[OSD([sQuery(id+"F63.wireOp",EDGE,"E54"),sQuery(id+"F63.wireOp",EDGE,"E55")])]});
            var Q3;
            Q3=makeQuery(id+"F64.opExtrude","CAP_EDGE",EDGE,{"disambiguationData":[OSD([sQuery(id+"F63.wireOp",EDGE,"E54")])],"isStart":false});
            var Q4;
            Q4=makeQuery(id+"F64.opExtrude","CAP_EDGE",EDGE,{"disambiguationData":[OSD([sQuery(id+"F63.wireOp",EDGE,"E54")])],"isStart":true});
            fillet(context, id + "F71", {"entities" : qUnion([Q0, Q1, Q2, Q3, Q4]), "radius" : 3 * mm, "tangentPropagation" : true, "allowEdgeOverflow" : false});
        }
        {
            var Q0;
            Q0=makeQuery(id+"F3.opLoft","CAP_FACE",FACE,{"disambiguationData":[OSD([makeQuery(id+"F2.imprint","IMPRINT",FACE,{"disambiguationData":[TD([[makeQuery(id+"F2.imprint","IMPRINT",EDGE,{"derivedFrom":sQuery(id+"F2.wireOp",EDGE,"E1.bottom")}),-1.0]])]})])],"isStart":true});
            var sketch = newSketch(context, id + "F72", { "sketchPlane" : qUnion([Q0])});
            skCircle(sketch, "E61", {"center": v(50, 50) * mm, "radius": 25 * mm});
            skSolve(sketch);
        }
        {
            var Q0;
            Q0=makeQuery(id+"F72.imprint","IMPRINT",FACE,{"disambiguationData":[TD([[makeQuery(id+"F72.imprint","IMPRINT",EDGE,{"derivedFrom":sQuery(id+"F72.wireOp",EDGE,"E61")}),-1.0]])]});
            extrude(context, id + "F73", {"entities" : qUnion([Q0]), "operationType" : NewBodyOperationType.ADD, "depth" : 25 * mm});
        }
        {
            var Q0;
            {var subQ0=sQuery(id+"F2.wireOp",EDGE,"E1.bottom");var subQ1=sQuery(id+"F2.wireOp",EDGE,"E1.top");var subQ2=sQuery(id+"F2.wireOp",EDGE,"E1.left");var subQ3=sQuery(id+"F2.wireOp",EDGE,"E1.right");Q0=makeQuery(id+"F73.opExtrude","CAP_FACE",FACE,{"disambiguationData":[OSD([sQuery(id+"F0.wireOp",EDGE,"E0.bottom"),sQuery(id+"F0.wireOp",EDGE,"E0.top"),sQuery(id+"F0.wireOp",EDGE,"E0.left"),sQuery(id+"F0.wireOp",EDGE,"E0.right"),subQ0,subQ1,subQ2,subQ3,makeQuery(id+"F2.imprint","IMPRINT",FACE,{"disambiguationData":[TD([[makeQuery(id+"F2.imprint","IMPRINT",EDGE,{"derivedFrom":subQ0}),-1.0]])]}),sQuery(id+"F72.wireOp",EDGE,"E61")])],"isStart":false});}
            fillet(context, id + "F74", {"entities" : qUnion([Q0]), "radius" : 2.5 * mm, "tangentPropagation" : true, "allowEdgeOverflow" : false});
        }
        {
            var Q0;
            Q0=makeQuery(id+"F57.opExtrude","SWEPT_FACE",FACE,{"disambiguationData":[OSD([sQuery(id+"F56.wireOp",EDGE,"E45.top")])]});
            var sketch = newSketch(context, id + "F75", { "sketchPlane" : qUnion([Q0])});
            skText(sketch, "E62", { "text": "IEM\n\n", "fontName": "OpenSans-Regular.ttf"});
            const initialGuessF75  = {"E62": [0.13356, 0.01172, 1, 0, 0.01056]};
            skSetInitialGuess(sketch, initialGuessF75);
            skSolve(sketch);
        }
        {
            var Q0;
            Q0=qSketchRegion(id+"F75",true);
            extrude(context, id + "F76", {"entities" : qUnion([Q0]), "operationType" : NewBodyOperationType.ADD, "depth" : 2 * mm});
        }
    });
